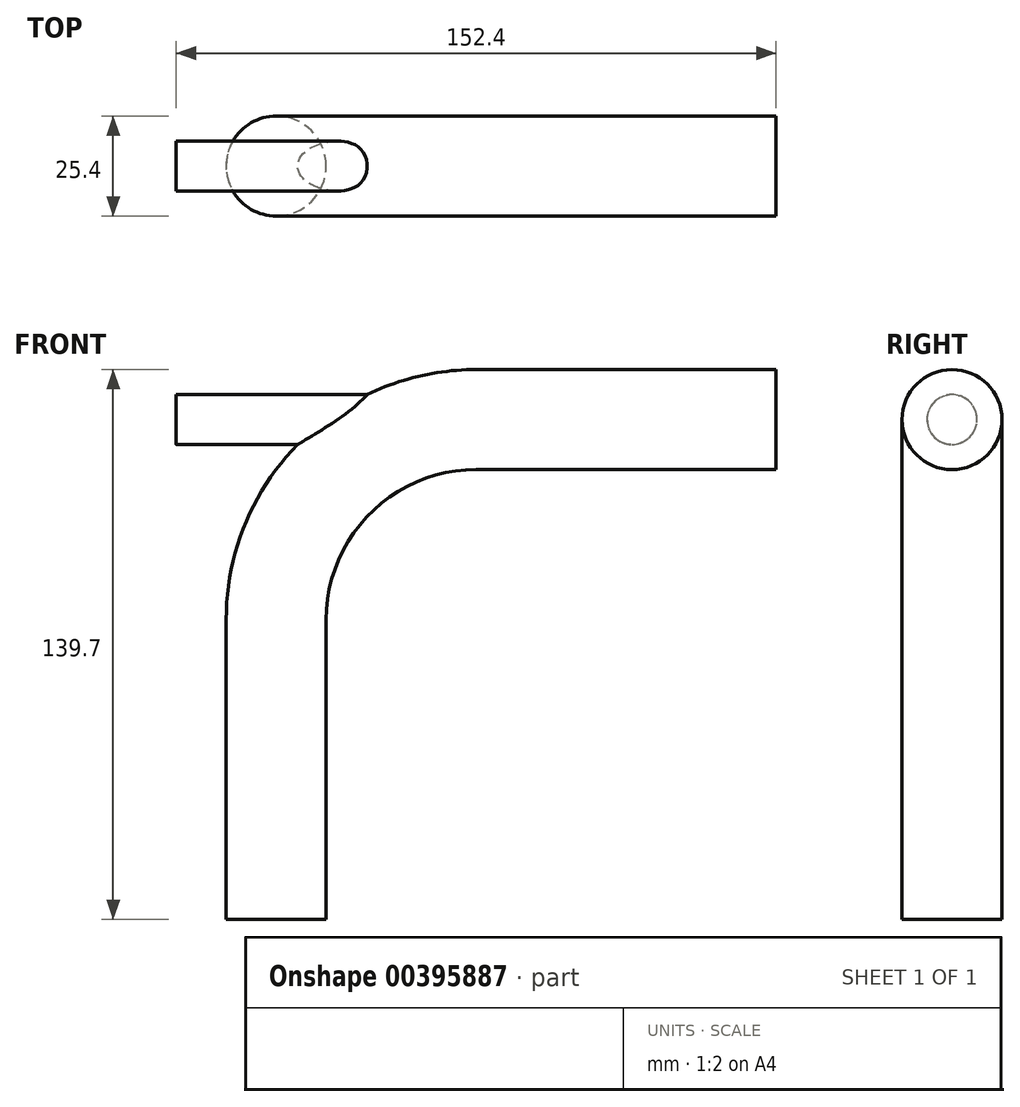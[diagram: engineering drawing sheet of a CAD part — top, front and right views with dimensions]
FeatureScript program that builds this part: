
annotation { "Feature Type Name" : "Feature", "Feature Type Description" : "" }
export const myFeature = defineFeature(function(context is Context, id is Id, definition is map)
    precondition{}
    {
        {
            var Q0;
            Q0=qCreatedBy(makeId("Front.planeOp"),FACE);
            var sketch = newSketch(context, id + "F0", { "sketchPlane" : qUnion([Q0])});
            skLineSegment(sketch, "E0", {"start": v(0, 0) * mm, "end": v(0, 76.2) * mm});
            skArc(sketch, "E1", {"start": v(50.8, 127) * mm, "mid": v(14.88, 112.12) * mm, "end": v(0, 76.2) * mm});
            skLineSegment(sketch, "E2", {"start": v(50.8, 127) * mm, "end": v(127, 127) * mm});
            skSolve(sketch);
        }
        {
            var Q0;
            Q0=qCreatedBy(makeId("Top.planeOp"),FACE);
            var sketch = newSketch(context, id + "F1", { "sketchPlane" : qUnion([Q0])});
            skCircle(sketch, "E3", {"center": v(0, 0) * mm, "radius": 12.7 * mm});
            skSolve(sketch);
        }
        {
            var Q0;
            Q0=makeQuery(id+"F1.imprint","IMPRINT",FACE,{"disambiguationData":[TD([[makeQuery(id+"F1.imprint","IMPRINT",EDGE,{"derivedFrom":sQuery(id+"F1.wireOp",EDGE,"E3")}),1.0]])]});
            var Q1;
            Q1 = qConstructionFilter(qBodyType(qCreatedBy(id + "F0" ,EDGE), BodyType.WIRE), ConstructionObject.NO);
            sweep(context, id + "F2", {"profiles" : qUnion([Q0]), "path" : qUnion([Q1])});
        }
        {
            var Q0;
            Q0=qCreatedBy(makeId("Right.planeOp"),FACE);
            cPlane(context, id + "F3", {"entities" : qUnion([Q0]), "cplaneType" : CPlaneType.OFFSET, "offset" : 25.4 * mm, "oppositeDirection" : true, "width" : 150 * mm, "height" : 150 * mm});
        }
        {
            var Q0;
            Q0=qCreatedBy(id+"F3.planeOp",FACE);
            var sketch = newSketch(context, id + "F4", { "sketchPlane" : qUnion([Q0])});
            skCircle(sketch, "E4", {"center": v(0, 127) * mm, "radius": 6.35 * mm});
            skSolve(sketch);
        }
        {
            var Q0;
            Q0 = qSketchRegion(id + "F4", true);
            extrude(context, id + "F5", {"entities" : qUnion([Q0]), "operationType" : NewBodyOperationType.ADD, "depth" : 3 * 25 * mm});
        }
    });
